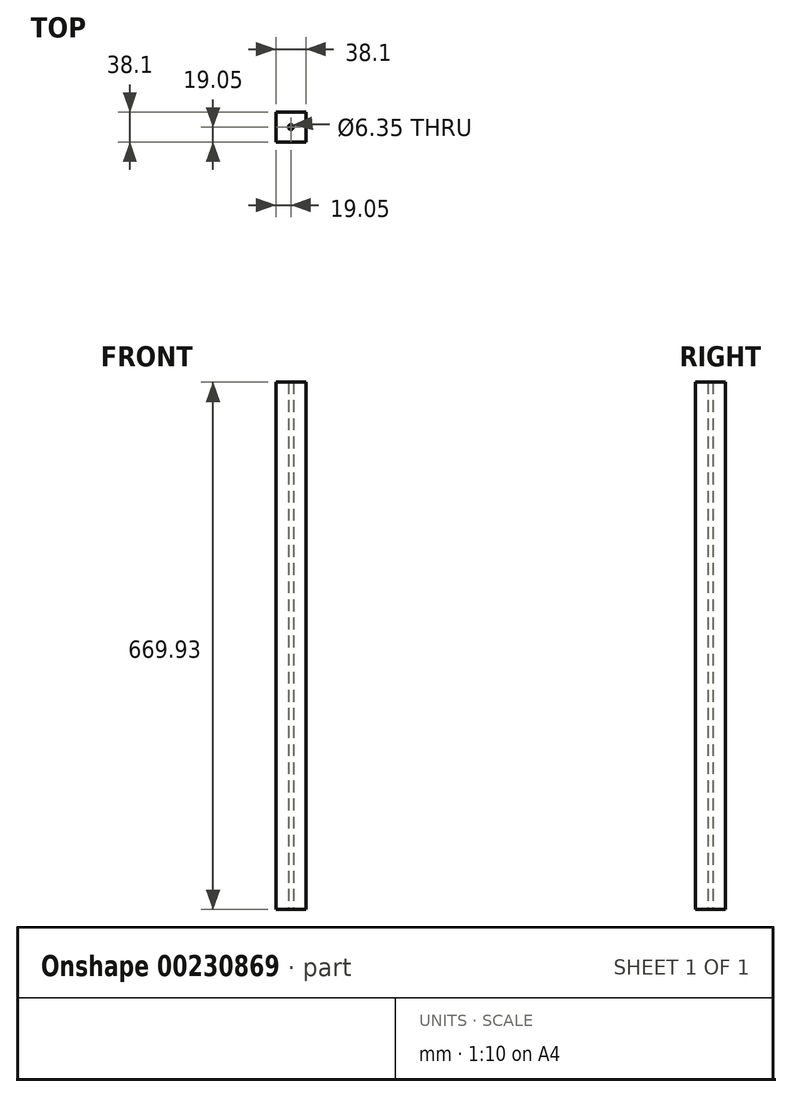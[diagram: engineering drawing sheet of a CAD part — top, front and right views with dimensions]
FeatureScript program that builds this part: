
annotation { "Feature Type Name" : "Feature", "Feature Type Description" : "" }
export const myFeature = defineFeature(function(context is Context, id is Id, definition is map)
    precondition{}
    {
        {
            var Q0;
            Q0=qCreatedBy(makeId("Top.planeOp"),FACE);
            var sketch = newSketch(context, id + "F0", { "sketchPlane" : qUnion([Q0])});
            skLineSegment(sketch, "E0.bottom", {"start": v(19.05, 19.05) * mm, "end": v(-19.05, 19.05) * mm});
            skLineSegment(sketch, "E0.top", {"start": v(19.05, -19.05) * mm, "end": v(-19.05, -19.05) * mm});
            skLineSegment(sketch, "E0.left", {"start": v(19.05, 19.05) * mm, "end": v(19.05, -19.05) * mm});
            skLineSegment(sketch, "E0.right", {"start": v(-19.05, 19.05) * mm, "end": v(-19.05, -19.05) * mm});
            skPoint(sketch, "E0.middle", {"position": v(0, 0) * mm});
            skCircle(sketch, "E1", {"center": v(0, 0) * mm, "radius": 3.18 * mm});
            skSolve(sketch);
        }
        {
            var Q0;
            Q0 = qSketchRegion(id + "F0", true);
            extrude(context, id + "F1", {"entities" : qUnion([Q0]), "depth" : 669.92 * mm});
        }
    });
